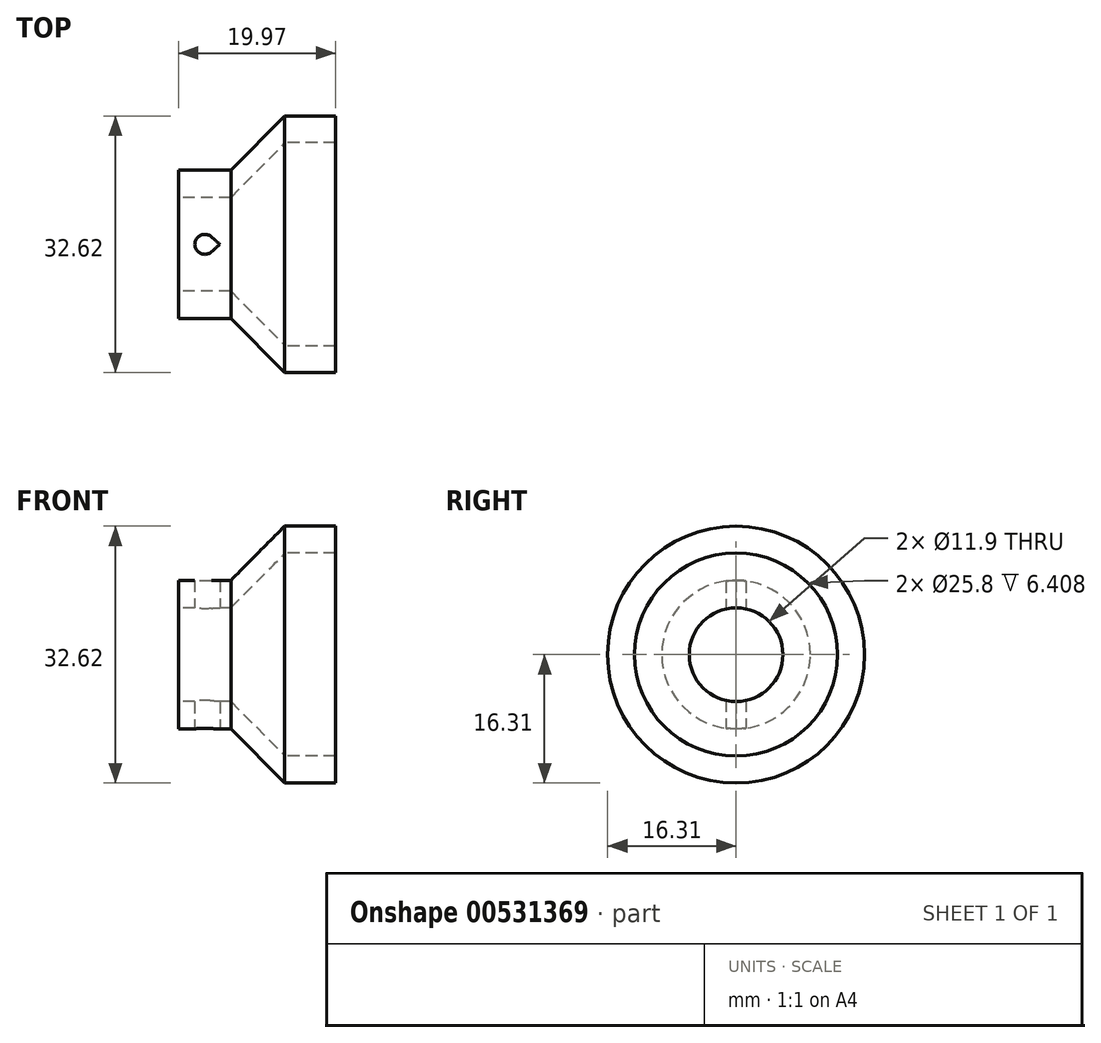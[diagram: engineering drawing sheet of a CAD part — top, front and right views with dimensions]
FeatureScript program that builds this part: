
annotation { "Feature Type Name" : "Feature", "Feature Type Description" : "" }
export const myFeature = defineFeature(function(context is Context, id is Id, definition is map)
    precondition{}
    {
        {
            var Q0;
            Q0=qCreatedBy(makeId("Top.planeOp"),FACE);
            var sketch = newSketch(context, id + "F0", { "sketchPlane" : qUnion([Q0])});
            skLineSegment(sketch, "E0.bottom", {"start": v(0, 0) * mm, "end": v(6.67, 0) * mm});
            skLineSegment(sketch, "E0.top", {"start": v(0, 5.95) * mm, "end": v(6.67, 5.95) * mm});
            skLineSegment(sketch, "E0.left", {"start": v(0, 0) * mm, "end": v(0, 5.95) * mm});
            skLineSegment(sketch, "E0.right", {"start": v(6.67, 0) * mm, "end": v(6.67, 5.95) * mm});
            skLineSegment(sketch, "E1.bottom", {"start": v(13.56, 0) * mm, "end": v(19.97, 0) * mm});
            skLineSegment(sketch, "E1.top", {"start": v(13.56, 12.9) * mm, "end": v(19.97, 12.9) * mm});
            skLineSegment(sketch, "E1.left", {"start": v(13.56, 0) * mm, "end": v(13.56, 12.9) * mm});
            skLineSegment(sketch, "E1.right", {"start": v(19.97, 0) * mm, "end": v(19.97, 12.9) * mm});
            skLineSegment(sketch, "E2", {"start": v(6.67, 5.95) * mm, "end": v(13.56, 12.9) * mm});
            skLineSegment(sketch, "E3", {"start": v(6.67, 0) * mm, "end": v(13.56, 0) * mm});
            skLineSegment(sketch, "E4", {"start": v(0, 0) * mm, "end": v(13.56, 0) * mm});
            skLineSegment(sketch, "E5", {"start": v(-9.95, 0) * mm, "end": v(44.13, 0) * mm, "construction": true});
            skLineSegment(sketch, "E6", {"start": v(0, 5.95) * mm, "end": v(0, 9.44) * mm});
            skLineSegment(sketch, "E7", {"start": v(0, 9.44) * mm, "end": v(6.67, 9.44) * mm});
            skLineSegment(sketch, "E8", {"start": v(6.67, 9.44) * mm, "end": v(13.49, 16.31) * mm});
            skLineSegment(sketch, "E9", {"start": v(13.49, 16.31) * mm, "end": v(19.97, 16.31) * mm});
            skLineSegment(sketch, "E10", {"start": v(19.97, 16.31) * mm, "end": v(19.97, 12.9) * mm});
            skSolve(sketch);
        }
        {
            var Q0;
            Q0=makeQuery(id+"F0.imprint","IMPRINT",FACE,{"disambiguationData":[TD([[makeQuery(id+"F0.imprint","IMPRINT",EDGE,{"derivedFrom":sQuery(id+"F0.wireOp",EDGE,"E0.top")}),1.0]])]});
            var Q1;
            Q1=sQuery(id+"F0.wireOp",EDGE,"E5");
            revolve(context, id + "F1", {"entities" : qUnion([Q0]), "axis" : qUnion([Q1]), "revolveType" : RevolveType.FULL});
        }
        {
            var Q0;
            Q0=qCreatedBy(makeId("Top.planeOp"),FACE);
            var sketch = newSketch(context, id + "F2", { "sketchPlane" : qUnion([Q0])});
            skCircle(sketch, "E11", {"center": v(3.36, 0) * mm, "radius": 1.27 * mm});
            skLineSegment(sketch, "E12", {"start": v(4.2, -0.95) * mm, "end": v(5.26, 0) * mm});
            skLineSegment(sketch, "E13", {"start": v(5.26, 0) * mm, "end": v(4.2, 0.95) * mm});
            skSolve(sketch);
        }
        {
            var Q0;
            Q0 = qSketchRegion(id + "F2", true);
            extrude(context, id + "F3", {"entities" : qUnion([Q0]), "operationType" : NewBodyOperationType.REMOVE, "endBound" : BoundingType.SYMMETRIC, "depth" : 100 * mm, "offsetDistance" : 25 * mm});
        }
    });
